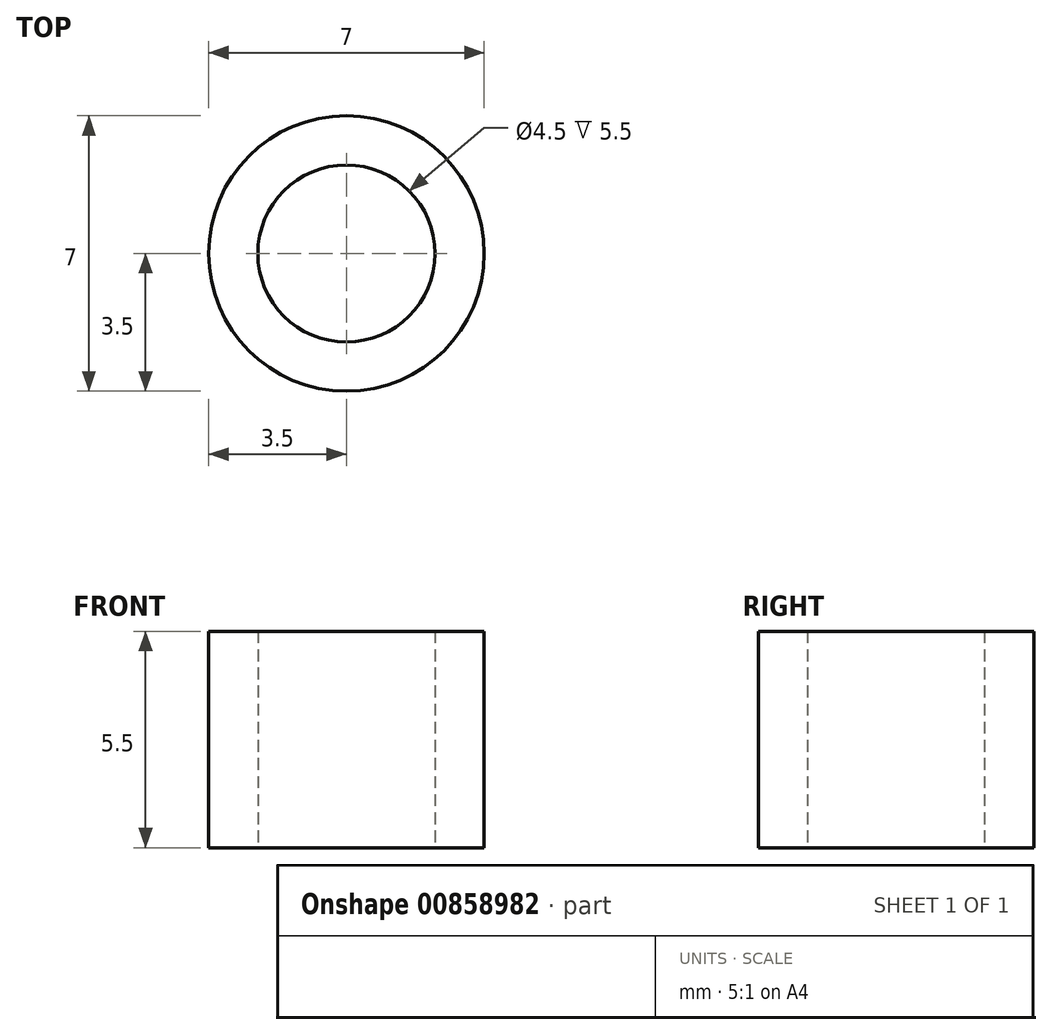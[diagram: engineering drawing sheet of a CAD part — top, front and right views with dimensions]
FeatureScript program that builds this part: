
annotation { "Feature Type Name" : "Feature", "Feature Type Description" : "" }
export const myFeature = defineFeature(function(context is Context, id is Id, definition is map)
    precondition{}
    {
        {
            var Q0;
            Q0=qCreatedBy(makeId("Top.planeOp"),FACE);
            var sketch = newSketch(context, id + "F0", { "sketchPlane" : qUnion([Q0])});
            skCircle(sketch, "E0", {"center": v(0, 0) * mm, "radius": 2.25 * mm});
            skCircle(sketch, "E1", {"center": v(0, 0) * mm, "radius": 3.5 * mm});
            skSolve(sketch);
        }
        {
            var Q0;
            Q0=makeQuery(id+"F0.imprint","IMPRINT",FACE,{"disambiguationData":[TD([[makeQuery(id+"F0.imprint","IMPRINT",EDGE,{"derivedFrom":sQuery(id+"F0.wireOp",EDGE,"E0")}),-1.0]])]});
            extrude(context, id + "F1", {"entities" : qUnion([Q0]), "depth" : 5.5 * mm, "offsetDistance" : 25.4 * mm});
        }
    });
